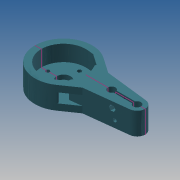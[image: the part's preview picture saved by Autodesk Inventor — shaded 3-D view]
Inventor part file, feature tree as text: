
AUTODESK INVENTOR PART (.ipt)
format: ipt  version: 2013 (Build 170138000, 138)  size: 339,456 bytes
history: native  units: mm
features: sketch x21, extrude x20, projected_geometry x4, mirror x2, chamfer x2, pattern_circular x1, fillet x1
ambient origin geometry x8: Origin, YZ Plane, XZ Plane, XY Plane, X Axis, Y Axis, Z Axis, Center Point
bodies: Solid1 (feature_tree)
feature tree (51):
  extrude  "Extrusion1"  Depth=25.0mm
  extrude  "Extrusion2"  Depth=12.0mm
  extrude  "Extrusion3"  Depth=40.0mm
  extrude  "Extrusion4"  Depth=10.0mm
  pattern_circular  "Circular Pattern1"  Count=4 Angle=360.0deg
  extrude  "Extrusion5"  Depth=4.0mm TaperAngle=0.0deg
  extrude  "Extrusion6"  Depth=7.0mm TaperAngle=0.0deg
  extrude  "Extrusion13"  Depth=6.5mm
  sketch  "Sketch14"  dims[d30=40.0mm d36=6.5mm]
  mirror  "Mirror1"
  extrude  "Extrusion14"  Depth=17.0mm
  extrude  "Extrusion15"  Depth=10.0mm
  extrude  "Extrusion16"  Depth=13.0mm TaperAngle=45.0deg
  extrude  "Extrusion17"  Depth=100.0mm TaperAngle=0.0deg
  extrude  "Extrusion18"  Depth=13.0mm TaperAngle=0.0deg
  extrude  "Extrusion19"  Depth=8.0mm
  fillet  "Fillet2"  Radius=63.662031mm
  extrude  "Extrusion21"  Depth=10000.0mm TaperAngle=0.0deg
  mirror  "Mirror2"
  extrude  "Extrusion22"  Depth=10.725mm
  extrude  "Extrusion8"  Depth=5.5mm
  extrude  "Extrusion9"  Depth=29.0mm TaperAngle=0.0deg
  chamfer  "Chamfer1"  Distance=25.475mm
  extrude  "Extrusion10"  Depth=5.5mm
  extrude  "Extrusion11"  Depth=29.0mm TaperAngle=0.0deg
  chamfer  "Chamfer2"  Distance=8.0mm
  extrude  "Extrusion12"  Depth=10000.0mm TaperAngle=0.0deg
  sketch  "Sketch1"  dims[d0=90.0mm d2=25.0mm]
  sketch  "Sketch2"  dims[d3=115.5mm d4=12.0mm]
  sketch  "Sketch3"  dims[d5=12.062153mm d6=40.0mm]
  sketch  "Sketch4"  dims[d7=35.0mm d8=0.0mm d9=10.0mm]
  sketch  "Sketch5"  dims[d10=25.0mm d11=0.0mm]
  sketch  "Sketch6"  dims[d12=25.0mm]
  sketch  "Sketch8"  dims[d13=3.5mm]
  sketch  "Sketch9"  dims[d14=25.0mm d15=0.0mm]
  sketch  "Sketch10"  dims[d16=5.5mm]
  sketch  "Sketch11"  dims[d17=4.0mm d18=0.0mm d19=40.0mm d20=360.0deg]
  sketch  "Sketch12"  dims[d22=15.0mm d24=4.0mm d25=0.0mm]
  sketch  "Sketch13"  dims[d26=22.0mm d28=7.0mm d29=0.0mm]
  sketch  "Sketch16"  dims[d37=5.5mm d38=17.0mm]
  sketch  "Sketch17"  dims[d39=10.0mm d40=0.0mm d41=10.0mm]
  sketch  "Sketch18"  dims[d43=13.0mm d44=0.0mm d45=13.0mm d46=2.0mm d47=45.0deg]
  sketch  "Sketch19"  dims[d48=8.0mm d49=100.0mm d50=5.0mm d51=0.0mm d52=0.0mm]
  sketch  "Sketch20"  dims[d53=10.0mm d55=13.0mm d56=0.0mm]
  sketch  "Sketch21"  dims[d57=13.0mm d58=2.0mm d59=45.0deg d60=8.0mm]
  sketch  "Sketch23"  dims[d61=10000.0mm d62=5.0mm d63=0.0mm d64=0.0mm d67=63.662031mm]
  projected_geometry  "Projected Loop1"
  sketch  "Sketch24"  dims[d69=6.0mm d70=10000.0mm d71=0.0mm d72=10.725mm d73=5.5mm d74=29.0mm d75=0.0mm d76=25.475mm d77=5.5mm d78=29.0mm d79=0.0mm d80=8.0mm d81=10000.0mm d82=5.0mm d83=0.0mm d84=0.0mm d85=8.0mm d86=10000.0mm d87=5.0mm d88=0.0mm d89=0.0mm d90=5.0mm d92=10000.0mm d93=0.0mm d94=2.0mm d96=10000.0mm d97=0.0mm d100=2.5mm d102=10.0mm d103=10.0mm d104=0.0mm d105=10.0mm d106=0.0mm d107=2.0mm]
  projected_geometry  "Projected Loop2"
  projected_geometry  "Projected Loop3"
  projected_geometry  "Project Cut Edges1"
